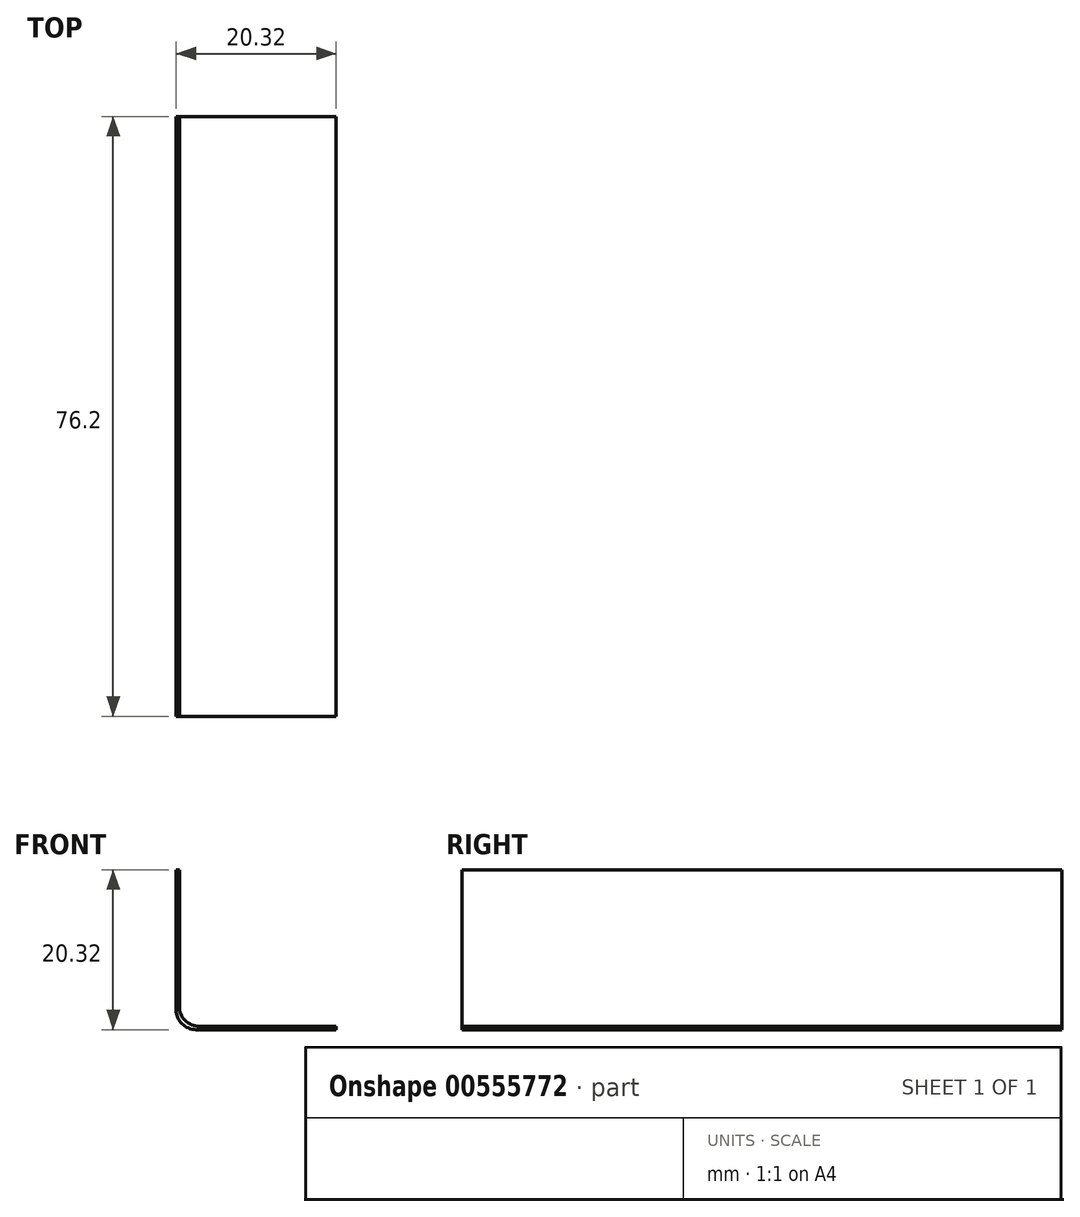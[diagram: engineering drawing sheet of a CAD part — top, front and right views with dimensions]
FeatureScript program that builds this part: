
annotation { "Feature Type Name" : "Feature", "Feature Type Description" : "" }
export const myFeature = defineFeature(function(context is Context, id is Id, definition is map)
    precondition{}
    {
        {
            var Q0;
            Q0=qCreatedBy(makeId("Front.planeOp"),FACE);
            var sketch = newSketch(context, id + "F0", { "sketchPlane" : qUnion([Q0])});
            skLineSegment(sketch, "E0", {"start": v(0, 0) * mm, "end": v(0, 20.32) * mm});
            skLineSegment(sketch, "E1", {"start": v(0, 0) * mm, "end": v(20.32, 0) * mm});
            skLineSegment(sketch, "E2.0", {"start": v(0.4, 0.4) * mm, "end": v(0.4, 20.32) * mm});
            skLineSegment(sketch, "E2.1", {"start": v(0.4, 0.4) * mm, "end": v(20.32, 0.4) * mm});
            skLineSegment(sketch, "E3", {"start": v(20.32, 0.4) * mm, "end": v(20.32, 0) * mm});
            skLineSegment(sketch, "E4", {"start": v(0, 20.32) * mm, "end": v(0.4, 20.32) * mm});
            skSolve(sketch);
        }
        {
            var Q0;
            Q0=makeQuery(id+"F0.imprint","IMPRINT",FACE,{"disambiguationData":[TD([[makeQuery(id+"F0.imprint","IMPRINT",EDGE,{"derivedFrom":sQuery(id+"F0.wireOp",EDGE,"E0")}),-1.0]])]});
            extrude(context, id + "F1", {"entities" : qUnion([Q0]), "depth" : 76.2 * mm, "offsetDistance" : 25.4 * mm});
        }
        {
            var Q0;
            Q0=makeQuery(id+"F1.opExtrude","SWEPT_EDGE",EDGE,{"disambiguationData":[OSD([sQuery(id+"F0.wireOp",EDGE,"E2.0"),sQuery(id+"F0.wireOp",EDGE,"E2.1")])]});
            var Q1;
            Q1=makeQuery(id+"F1.opExtrude","SWEPT_EDGE",EDGE,{"disambiguationData":[OSD([sQuery(id+"F0.wireOp",EDGE,"E0"),sQuery(id+"F0.wireOp",EDGE,"E1")])]});
            fillet(context, id + "F2", {"entities" : qUnion([Q0, Q1]), "radius" : 2.54 * mm, "tangentPropagation" : true, "allowEdgeOverflow" : false});
        }
    });
